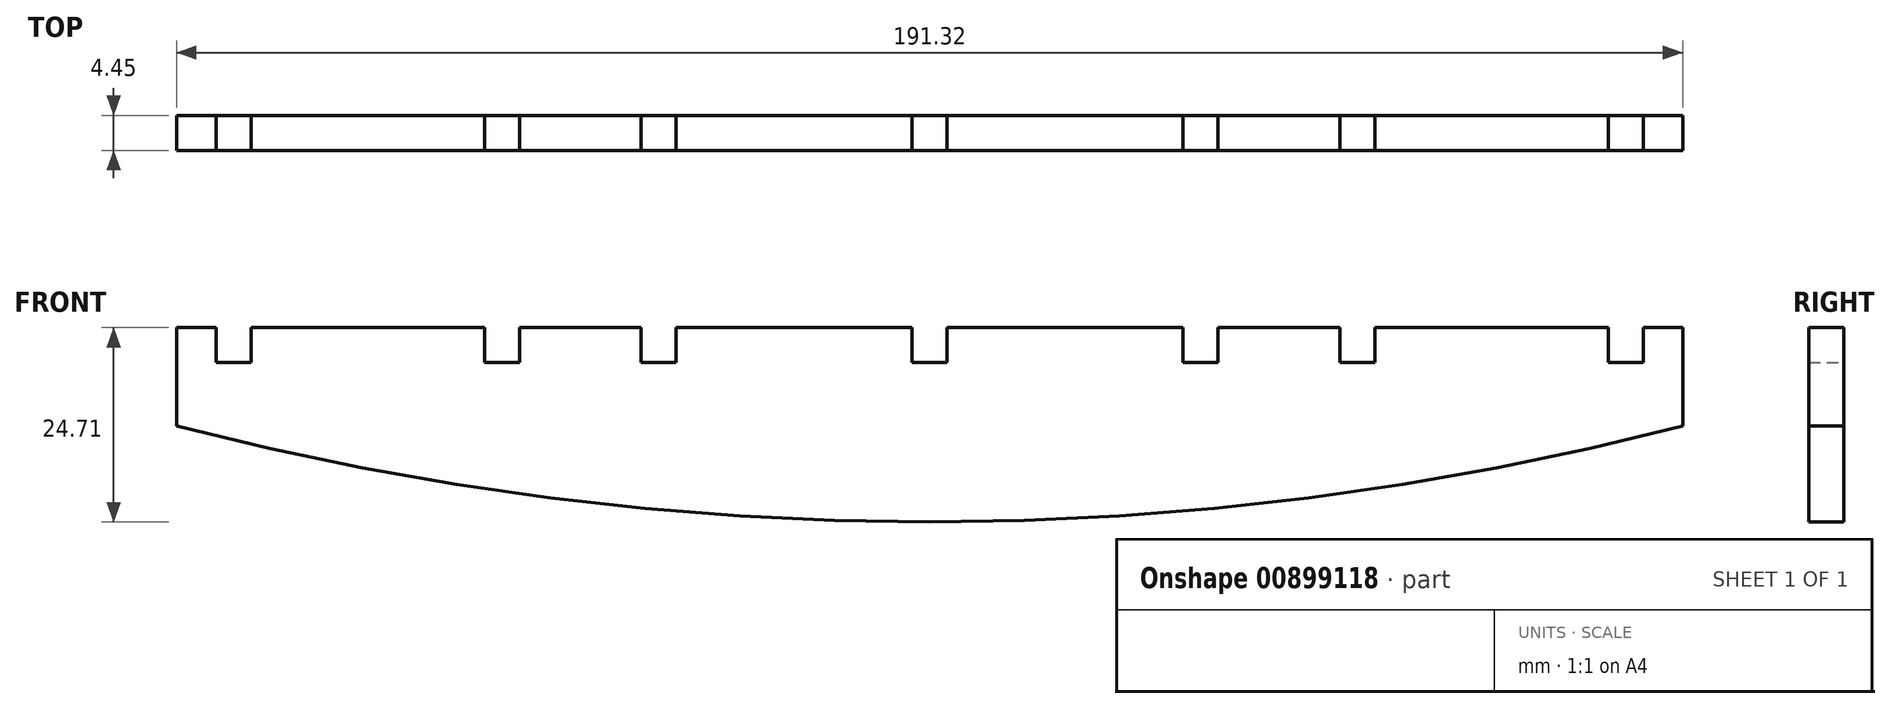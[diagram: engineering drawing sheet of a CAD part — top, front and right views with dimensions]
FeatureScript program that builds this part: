
annotation { "Feature Type Name" : "Feature", "Feature Type Description" : "" }
export const myFeature = defineFeature(function(context is Context, id is Id, definition is map)
    precondition{}
    {
        {
            var Q0;
            Q0=qCreatedBy(makeId("Front.planeOp"),FACE);
            var sketch = newSketch(context, id + "F0", { "sketchPlane" : qUnion([Q0])});
            skLineSegment(sketch, "E0.bottom", {"start": v(2.22, 88.9) * mm, "end": v(-2.23, 88.9) * mm});
            skLineSegment(sketch, "E0.left", {"start": v(2.22, 88.9) * mm, "end": v(2.22, 93.35) * mm});
            skLineSegment(sketch, "E0.right", {"start": v(-2.23, 88.9) * mm, "end": v(-2.23, 93.35) * mm});
            skPoint(sketch, "E0.middle", {"position": v(0, 91.12) * mm});
            skPoint(sketch, "E1.orphan", {"position": v(0, 0) * mm});
            skLineSegment(sketch, "E2.bottom", {"start": v(-52.11, 88.9) * mm, "end": v(-56.56, 88.9) * mm});
            skLineSegment(sketch, "E2.left", {"start": v(-52.11, 88.9) * mm, "end": v(-52.11, 93.35) * mm});
            skLineSegment(sketch, "E2.right", {"start": v(-56.56, 88.9) * mm, "end": v(-56.56, 93.35) * mm});
            skPoint(sketch, "E2.middle", {"position": v(-54.34, 91.13) * mm});
            skLineSegment(sketch, "E3.MirrorCS", {"start": v(52.11, 88.9) * mm, "end": v(56.56, 88.9) * mm});
            skLineSegment(sketch, "E4.MirrorCS", {"start": v(56.56, 88.9) * mm, "end": v(56.56, 93.35) * mm});
            skLineSegment(sketch, "E5.MirrorCS", {"start": v(52.11, 88.9) * mm, "end": v(52.11, 93.35) * mm});
            skLineSegment(sketch, "E6.bottom", {"start": v(-32.18, 88.9) * mm, "end": v(-36.63, 88.9) * mm});
            skLineSegment(sketch, "E6.left", {"start": v(-32.18, 88.9) * mm, "end": v(-32.18, 93.35) * mm});
            skLineSegment(sketch, "E6.right", {"start": v(-36.63, 88.9) * mm, "end": v(-36.63, 93.35) * mm});
            skPoint(sketch, "E6.middle", {"position": v(-34.4, 91.13) * mm});
            skLineSegment(sketch, "E7.MirrorCS", {"start": v(32.18, 88.9) * mm, "end": v(32.18, 93.35) * mm});
            skLineSegment(sketch, "E8.MirrorCS", {"start": v(32.18, 88.9) * mm, "end": v(36.63, 88.9) * mm});
            skLineSegment(sketch, "E9.MirrorCS", {"start": v(36.63, 88.9) * mm, "end": v(36.63, 93.35) * mm});
            skLineSegment(sketch, "E10.bottom", {"start": v(-90.66, 88.9) * mm, "end": v(-86.2, 88.9) * mm});
            skLineSegment(sketch, "E10.left", {"start": v(-90.66, 88.9) * mm, "end": v(-90.66, 93.35) * mm});
            skLineSegment(sketch, "E10.right", {"start": v(-86.2, 88.9) * mm, "end": v(-86.2, 93.35) * mm});
            skLineSegment(sketch, "E11.MirrorCS", {"start": v(90.66, 88.9) * mm, "end": v(86.2, 88.9) * mm});
            skLineSegment(sketch, "E12.MirrorCS", {"start": v(86.2, 88.9) * mm, "end": v(86.2, 93.35) * mm});
            skLineSegment(sketch, "E13.MirrorCS", {"start": v(90.66, 88.9) * mm, "end": v(90.66, 93.35) * mm});
            skLineSegment(sketch, "E14", {"start": v(-86.2, 93.35) * mm, "end": v(-56.56, 93.35) * mm});
            skLineSegment(sketch, "E15", {"start": v(-52.11, 93.35) * mm, "end": v(-36.63, 93.35) * mm});
            skLineSegment(sketch, "E16", {"start": v(-32.18, 93.35) * mm, "end": v(-2.23, 93.35) * mm});
            skLineSegment(sketch, "E17", {"start": v(2.22, 93.35) * mm, "end": v(32.18, 93.35) * mm});
            skLineSegment(sketch, "E18", {"start": v(36.63, 93.35) * mm, "end": v(52.11, 93.35) * mm});
            skLineSegment(sketch, "E19", {"start": v(86.2, 93.35) * mm, "end": v(56.56, 93.35) * mm});
            skLineSegment(sketch, "E20", {"start": v(-90.66, 93.35) * mm, "end": v(-95.66, 93.35) * mm});
            skLineSegment(sketch, "E21.MirrorCS", {"start": v(90.66, 93.35) * mm, "end": v(95.66, 93.35) * mm});
            skLineSegment(sketch, "E22", {"start": v(-95.66, 93.35) * mm, "end": v(-95.66, 80.85) * mm});
            skLineSegment(sketch, "E23.MirrorCS", {"start": v(95.66, 93.35) * mm, "end": v(95.66, 80.85) * mm});
            skArc(sketch, "E24", {"start": v(-95.66, 80.85) * mm, "mid": v(0, 68.64) * mm, "end": v(95.66, 80.85) * mm});
            skSolve(sketch);
        }
        {
            var Q0;
            Q0=makeQuery(id+"F0.imprint","IMPRINT",FACE,{"disambiguationData":[TD([[makeQuery(id+"F0.imprint","IMPRINT",EDGE,{"derivedFrom":sQuery(id+"F0.wireOp",EDGE,"E0.bottom")}),1.0]])]});
            extrude(context, id + "F1", {"entities" : qUnion([Q0]), "depth" : 4.45 * mm, "offsetDistance" : 25 * mm});
        }
    });
